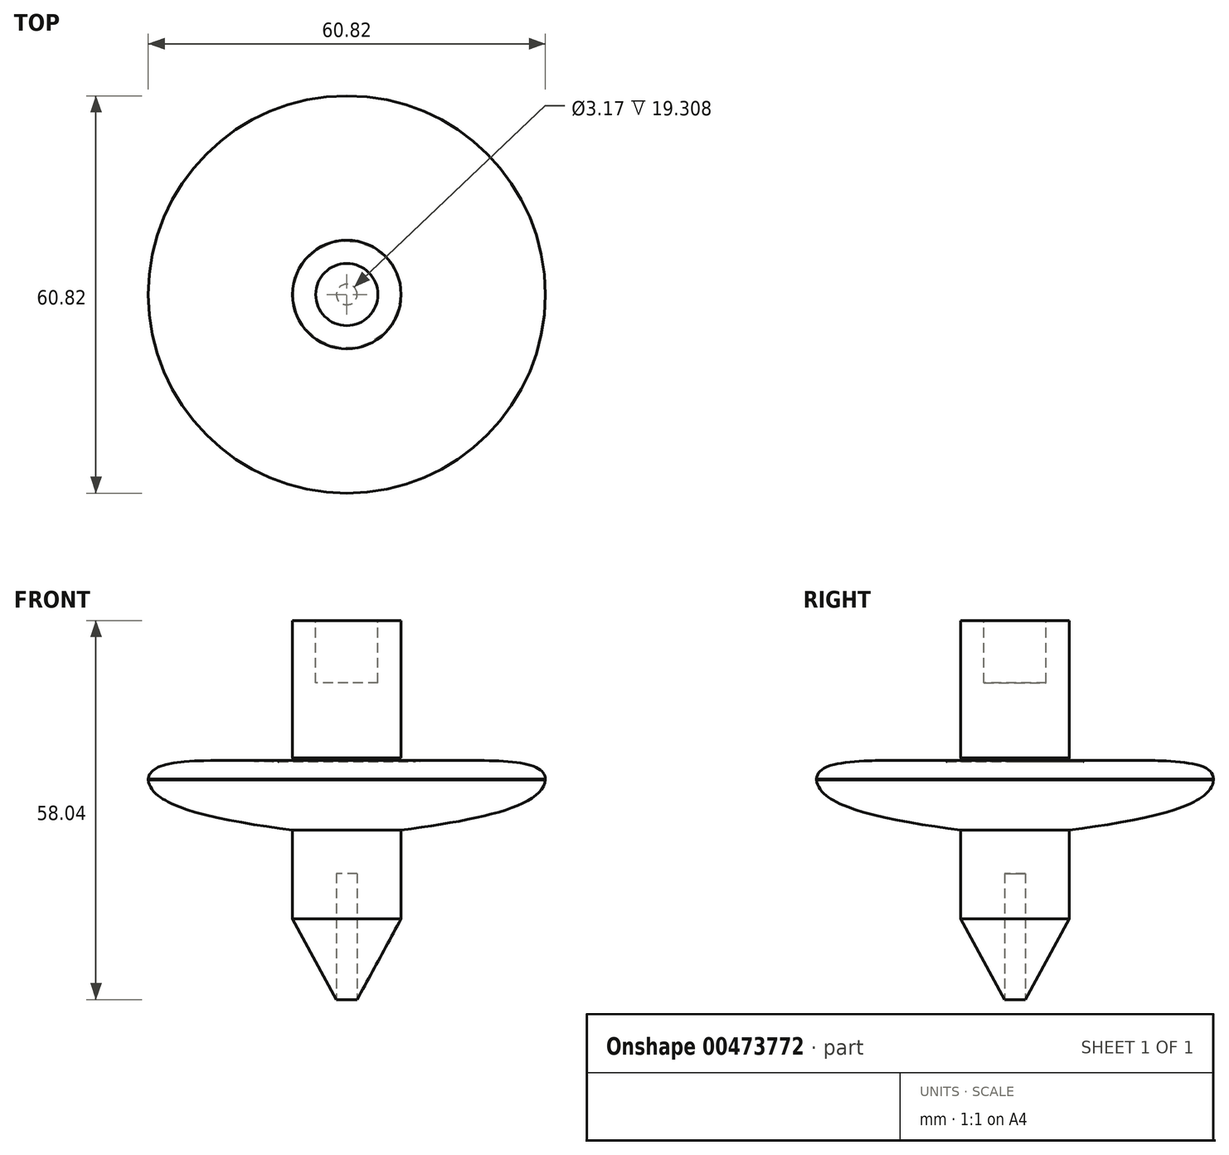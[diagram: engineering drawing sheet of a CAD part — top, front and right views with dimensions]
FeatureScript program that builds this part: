
annotation { "Feature Type Name" : "Feature", "Feature Type Description" : "" }
export const myFeature = defineFeature(function(context is Context, id is Id, definition is map)
    precondition{}
    {
        {
            var Q0;
            Q0=qCreatedBy(makeId("Front.planeOp"),FACE);
            var sketch = newSketch(context, id + "F0", { "sketchPlane" : qUnion([Q0])});
            skLineSegment(sketch, "E0", {"start": v(0, 0) * mm, "end": v(8.32, 15.28) * mm});
            skLineSegment(sketch, "E1", {"start": v(8.32, 15.28) * mm, "end": v(8.32, 28.84) * mm});
            skFitSpline(sketch, "E2", {"points": [v(8.32, 28.84) * mm, v(29.69, 34.9) * mm, v(28.97, 38.48) * mm, v(8.32, 39.55) * mm, v(8.32, 39.9) * mm], "startDerivative": vector(77.71, 10.67) * mm, "endDerivative": vector(5, 8.16) * mm});
            skLineSegment(sketch, "E3", {"start": v(8.32, 39.9) * mm, "end": v(8.32, 60.96) * mm});
            skLineSegment(sketch, "E4", {"start": v(8.32, 60.96) * mm, "end": v(0, 60.96) * mm});
            skLineSegment(sketch, "E5", {"start": v(0, 60.96) * mm, "end": v(0, 0) * mm});
            skLineSegment(sketch, "E6", {"start": v(30.41, 36.58) * mm, "end": v(30.41, 41.44) * mm});
            skLineSegment(sketch, "E7", {"start": v(30.41, 36.58) * mm, "end": v(30.41, 32.5) * mm});
            skSolve(sketch);
        }
        {
            var Q0;
            Q0=makeQuery(id+"F0.imprint","IMPRINT",FACE,{"disambiguationData":[TD([[makeQuery(id+"F0.imprint","IMPRINT",EDGE,{"derivedFrom":sQuery(id+"F0.wireOp",EDGE,"E0")}),1.0]])]});
            var Q1;
            Q1=sQuery(id+"F0.wireOp",EDGE,"E5");
            revolve(context, id + "F1", {"entities" : qUnion([Q0]), "axis" : qUnion([Q1]), "revolveType" : RevolveType.FULL});
        }
        {
            var Q0;
            Q0=makeQuery(id+"F1.opRevolve","SWEPT_FACE",FACE,{"disambiguationData":[OSD([sQuery(id+"F0.wireOp",EDGE,"E4")])]});
            var sketch = newSketch(context, id + "F2", { "sketchPlane" : qUnion([Q0])});
            skCircle(sketch, "E8", {"center": v(0, 0) * mm, "radius": 4.76 * mm});
            skSolve(sketch);
        }
        {
            var Q0;
            Q0=makeQuery(id+"F2.imprint","IMPRINT",FACE,{"disambiguationData":[TD([[makeQuery(id+"F2.imprint","IMPRINT",EDGE,{"derivedFrom":sQuery(id+"F2.wireOp",EDGE,"E8")}),1.0]])]});
            extrude(context, id + "F3", {"entities" : qUnion([Q0]), "operationType" : NewBodyOperationType.REMOVE, "depth" : -9.52 * mm});
        }
        {
            var Q0;
            Q0=makeQuery(id+"F2.imprint","IMPRINT",FACE,{"disambiguationData":[TD([[makeQuery(id+"F2.imprint","IMPRINT",EDGE,{"derivedFrom":sQuery(id+"F2.wireOp",EDGE,"E8")}),1.0]])]});
            extrude(context, id + "F4", {"entities" : qUnion([Q0]), "oppositeDirection" : true, "depth" : 9.52 * mm});
        }
        {
            var Q0;
            Q0=qCreatedBy(makeId("Top.planeOp"),FACE);
            var sketch = newSketch(context, id + "F5", { "sketchPlane" : qUnion([Q0])});
            skCircle(sketch, "E9", {"center": v(0, 0) * mm, "radius": 1.59 * mm});
            skSolve(sketch);
        }
        {
            var Q0;
            Q0=qSketchRegion(id+"F5",true);
            extrude(context, id + "F6", {"entities" : qUnion([Q0]), "operationType" : NewBodyOperationType.REMOVE, "depth" : 22.22 * mm});
        }
    });
